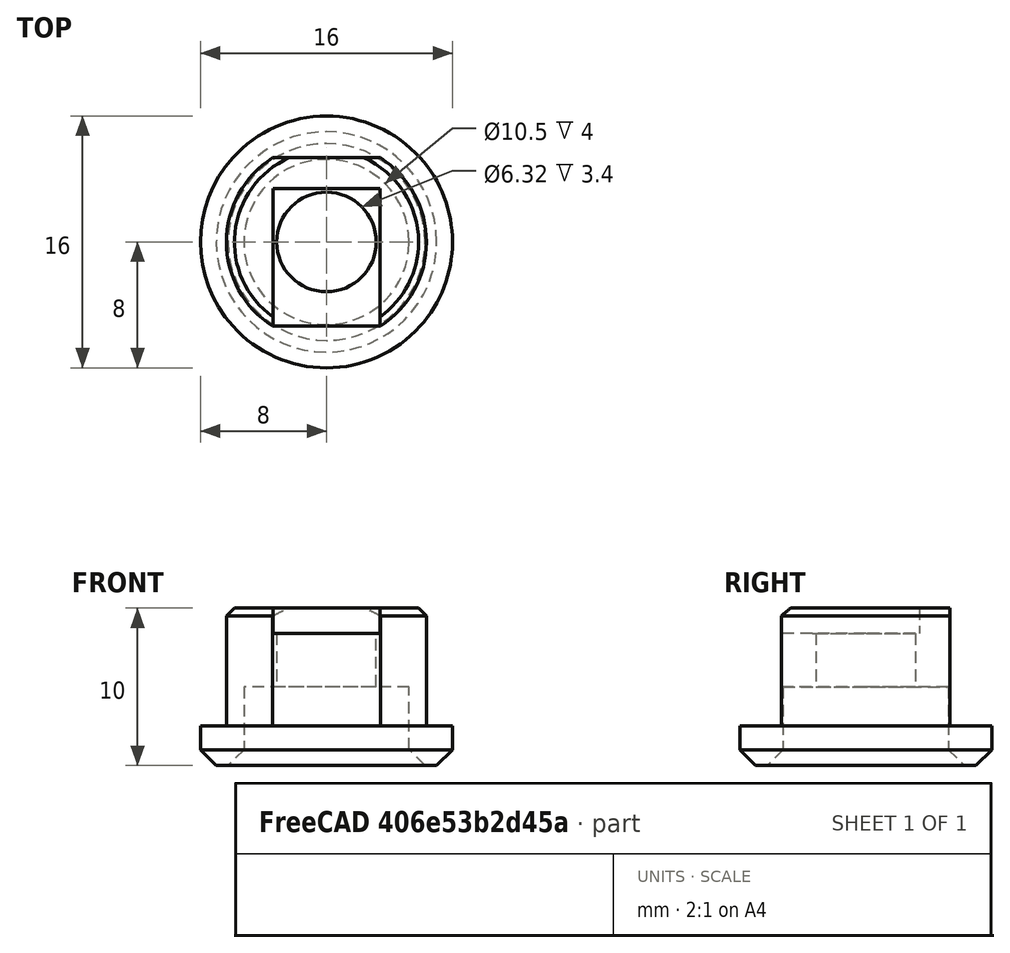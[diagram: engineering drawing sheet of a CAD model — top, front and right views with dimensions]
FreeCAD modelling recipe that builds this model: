
FCSTD DOCUMENT  (FreeCAD 1.1R44874 (Git))
Label: suporte-antena-lateral
License: All rights reserved
LicenseURL: http://en.wikipedia.org/wiki/All_rights_reserved
objects: Sketcher::SketchObject×5, PartDesign::Pocket×4, PartDesign::Chamfer×3, PartDesign::Pad×2, PartDesign::Body×1, App::Point×1
note: 38 computed .brp shape members not serialized (recipe doc carries the construction recipe); baked Part::Feature solids carry a one-line shape summary decoded from their .brp

FEATURE [Sketcher::SketchObject] Sketch
  ArcFitTolerance = 0
  AttachmentSupport = -> [XY_Plane]
  ExternalTypes = [0]
  FullyConstrained = true
  MakeInternals = false
  MapMode = 5
  _ExternalGeoVersion = 0
  sketch-geometry (2):
    g0: Circle CenterX=0 CenterY=0 CenterZ=0 NormalX=0 NormalY=0 NormalZ=1 AngleXU=0 Radius=8
    g1: Circle CenterX=0 CenterY=0 CenterZ=0 NormalX=0 NormalY=0 NormalZ=1 AngleXU=0 Radius=3.16
  constraints (4):
    c: Coincident(g0,g-1)
    c: Coincident(g1,g0)
    c: Diameter(g1) = 6.32
    c: Diameter(g0) = 16
FEATURE [PartDesign::Pad] Pad
  Direction = (0,0,1)
  Length = 2.5
  Length2 = 10
  Profile = -> Sketch
  ReferenceAxis = -> Sketch [N_Axis]
  SideType = 0
  Suppressed = false
  Type = 0
  Type2 = 0
FEATURE [Sketcher::SketchObject] Sketch001
  ArcFitTolerance = 0
  AttachmentSupport = -> [Pad]
  ExternalGeometry = -> [Pad]
  ExternalTypes = [0]
  FullyConstrained = true
  MakeInternals = false
  MapMode = 5
  Placement = pos=(0,0,2.5) rot=(0,0,1;0rad)
  _ExternalGeoVersion = 0
  sketch-geometry (2):
    g0: Circle CenterX=0 CenterY=0 CenterZ=0 NormalX=0 NormalY=0 NormalZ=1 AngleXU=0 Radius=6.35
    g1: Circle CenterX=0 CenterY=0 CenterZ=0 NormalX=0 NormalY=0 NormalZ=1 AngleXU=0 Radius=3.16
  constraints (4):
    c: Coincident(g0,g-1)
    c: Diameter(g0) = 12.7
    c: Coincident(g1,g0)
    c: Equal(g-3,g1)
FEATURE [PartDesign::Pad] Pad001
  BaseFeature = -> Pad
  Direction = (0,0,1)
  Length = 7.5
  Length2 = 10
  Profile = -> Sketch001
  ReferenceAxis = -> Sketch001 [N_Axis]
  SideType = 0
  Suppressed = false
  Type = 0
  Type2 = 0
FEATURE [Sketcher::SketchObject] Sketch002
  ArcFitTolerance = 0
  AttachmentSupport = -> [Pad001]
  ExternalTypes = [0]
  FullyConstrained = true
  MakeInternals = false
  MapMode = 5
  Placement = pos=(0,0,0) rot=(1,0,0;3.14159rad)
  _ExternalGeoVersion = 0
  sketch-geometry (1):
    g0: Circle CenterX=0 CenterY=0 CenterZ=0 NormalX=0 NormalY=0 NormalZ=1 AngleXU=0 Radius=5.25
  constraints (2):
    c: Coincident(g0,g-1)
    c: Diameter(g0) = 10.5
FEATURE [PartDesign::Pocket] Pocket
  BaseFeature = -> Pad001
  Direction = (0,0,1)
  Length = 5
  Length2 = 5
  Profile = -> Sketch002
  ReferenceAxis = -> Sketch002 [N_Axis]
  SideType = 0
  Suppressed = false
  Type = 0
  Type2 = 0
FEATURE [Sketcher::SketchObject] Sketch003
  ArcFitTolerance = 0
  AttachmentSupport = -> [Pocket]
  ExternalGeometry = -> [Pocket]
  ExternalTypes = [0]
  FullyConstrained = true
  MakeInternals = false
  MapMode = 5
  Placement = pos=(0,0,10) rot=(0,0,1;0rad)
  _ExternalGeoVersion = 0
  sketch-geometry (9):
    g0: LineSegment StartX=-5.9479 StartY=8 StartZ=0 EndX=5.9479 EndY=8 EndZ=0
    g1: LineSegment StartX=5.9479 StartY=8 StartZ=0 EndX=5.9479 EndY=5.35 EndZ=0
    g2: LineSegment StartX=5.9479 StartY=5.35 StartZ=0 EndX=-5.9479 EndY=5.35 EndZ=0
    g3: LineSegment StartX=-5.9479 StartY=5.35 StartZ=0 EndX=-5.9479 EndY=8 EndZ=0
    g4: LineSegment StartX=-5.9479 StartY=-5.35 StartZ=0 EndX=5.9479 EndY=-5.35 EndZ=0
    g5: LineSegment StartX=5.9479 StartY=-5.35 StartZ=0 EndX=5.9479 EndY=-8 EndZ=0
    g6: LineSegment StartX=5.9479 StartY=-8 StartZ=0 EndX=-5.9479 EndY=-8 EndZ=0
    g7: LineSegment StartX=-5.9479 StartY=-8 StartZ=0 EndX=-5.9479 EndY=-5.35 EndZ=0
    g8: GeomPoint [constr] X=0 Y=-6.35 Z=0
  constraints (24):
    c: Coincident(g0,g1)
    c: Coincident(g1,g2)
    c: Coincident(g2,g3)
    c: Coincident(g3,g0)
    c: Horizontal(g2)
    c: Vertical(g1)
    c: Vertical(g3)
    c: Coincident(g4,g5)
    c: Coincident(g5,g6)
    c: Coincident(g6,g7)
    c: Coincident(g7,g4)
    c: Horizontal(g4)
    c: Vertical(g5)
    c: Vertical(g7)
    c: Symmetric(g5,g6,g-2)
    c: Symmetric(g0,g0,g-2)
    c: Tangent(g0,g-3)
    c: PointOnObject(g1,g-3)
    c: PointOnObject(g4,g-3)
    c: Tangent(g6,g-3)
    c: Equal(g6,g0)
    c: PointOnObject(g8,g-4)
    c: PointOnObject(g8,g-2)
    c: DistanceY(g8,g4) = 1
FEATURE [PartDesign::Pocket] Pocket001
  BaseFeature = -> Pocket
  Direction = (0,0,-1)
  Length = 0
  Length2 = 5
  Profile = -> Sketch003
  ReferenceAxis = -> Sketch003 [N_Axis]
  SideType = 0
  Suppressed = false
  Type = 3
  Type2 = 0
  UpToFace = -> Pocket [Face3]
FEATURE [Sketcher::SketchObject] Sketch004
  ArcFitTolerance = 0
  AttachmentSupport = -> [Pocket001]
  ExternalTypes = [0]
  FullyConstrained = true
  MakeInternals = false
  MapMode = 5
  Placement = pos=(0,0,5) rot=(1,0,0;3.14159rad)
  _ExternalGeoVersion = 0
  sketch-geometry (5):
    g0: LineSegment StartX=-3.4 StartY=3.4 StartZ=0 EndX=3.4 EndY=3.4 EndZ=0
    g1: LineSegment StartX=3.4 StartY=3.4 StartZ=0 EndX=3.4 EndY=-3.4 EndZ=0
    g2: LineSegment StartX=3.4 StartY=-3.4 StartZ=0 EndX=-3.4 EndY=-3.4 EndZ=0
    g3: LineSegment StartX=-3.4 StartY=-3.4 StartZ=0 EndX=-3.4 EndY=3.4 EndZ=0
    g4: Circle [constr] CenterX=0 CenterY=0 CenterZ=0 NormalX=0 NormalY=0 NormalZ=1 AngleXU=0 Radius=3.4
  constraints (14):
    c: Coincident(g0,g1)
    c: Coincident(g1,g2)
    c: Coincident(g2,g3)
    c: Coincident(g3,g0)
    c: Horizontal(g0)
    c: Horizontal(g2)
    c: Vertical(g1)
    c: Vertical(g3)
    c: Coincident(g4,g-1)
    c: Tangent(g4,g0)
    c: Tangent(g4,g3)
    c: Tangent(g2,g4)
    c: Tangent(g1,g4)
    c: DistanceX(g0,g0) = 6.8
FEATURE [PartDesign::Pocket] Pocket002
  BaseFeature = -> Pocket001
  Direction = (0,0,1)
  Length = 1.6
  Length2 = 5
  Profile = -> Sketch004
  ReferenceAxis = -> Sketch004 [N_Axis]
  SideType = 0
  Suppressed = false
  Type = 0
  Type2 = 0
FEATURE [PartDesign::Pocket] Pocket003
  BaseFeature = -> Pocket002
  Direction = (1,0,0)
  Length = 5
  Length2 = 5
  Profile = -> Pocket002 [Face18]
  SideType = 0
  Suppressed = false
  Type = 1
  Type2 = 0
FEATURE [PartDesign::Chamfer] Chamfer
  Angle = 45
  Base = -> Pocket003 [Edge27,Edge24,Edge21]
  BaseFeature = -> Pocket003
  ChamferType = 0
  FlipDirection = false
  Size = 0.5
  Size2 = 1
  SupportTransform = false
  Suppressed = false
  UseAllEdges = false
FEATURE [PartDesign::Chamfer] Chamfer001
  Angle = 45
  Base = -> Chamfer [Edge58]
  BaseFeature = -> Chamfer
  ChamferType = 0
  FlipDirection = false
  Size = 1
  Size2 = 1
  SupportTransform = false
  Suppressed = false
  UseAllEdges = false
FEATURE [PartDesign::Chamfer] Chamfer002
  Angle = 45
  Base = -> Chamfer001 [Edge2]
  BaseFeature = -> Chamfer001
  ChamferType = 0
  FlipDirection = false
  Size = 1
  Size2 = 1
  SupportTransform = false
  Suppressed = false
  UseAllEdges = false
FEATURE [PartDesign::Body] Body
  AllowCompound = false
  Group = -> [Sketch,Pad,Sketch001,Pad001,Sketch002,Pocket,Sketch003,Pocket001,Sketch004,Pocket002,Pocket003,Chamfer,Chamfer001,Chamfer002]
  Origin = -> Origin
  Tip = -> Chamfer002
FEATURE [App::Point] Origin001  label="Origem"
  Role = Origin
